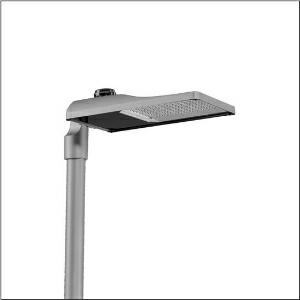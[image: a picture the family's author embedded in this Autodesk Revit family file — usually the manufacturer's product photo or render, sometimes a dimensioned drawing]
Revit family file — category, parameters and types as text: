
# Revit family: streetlight_sl_31_maxi___st1_5a_5xh8p7bn08sa_f059
name_source: partatom
category: Lighting Fixtures
units: mm (PartAtom-declared; Revit-internal decimal feet)

## family parameters
Cut with Voids When Loaded = No
Host = Face
Light Source = No
Part Type = Normal
Room Calculation Point = No
Round Connector Dimension = Use Diameter
Shared = No

## types (1)
- --- (1 x LED, 22010 lm, 208.6 W, 2200K)
    Apparent Load = 209 VA
    CIE Flux Codes = 22 53 95 100 100
    Color Rendering = 70
    Color Temperature = 2200K
    Default Elevation = 1800 mm
    Description = Streetlight SL 31 maxi NEMA (7pin) mast luminaire for post-top, side-entry; light control with lens of PMMA; light distribution: ST1.5a, direct asymmetric distribution, for standard-compliant lighting for roads and squares; LED: luminous flux: 22.010lm, light colour: 722, colour temperature: 2200K; luminous efficacy: 105,5lm/W; control: pre-setting: linear dimming characteristic, flexible luminous flux parameterisation, time-dependent luminous flux control, constant luminous flux control, intelligent temperature release in ECG and LED module, overheat protection; luminaire housing, of diecast aluminium, SITECO metallic grey (DB 702S), corrosivity category C5 high according to DIN EN ISO 12944; cover of toughened safety glass, transparent, opened without tools; mast flange of diecast aluminium, SITECO metallic grey (DB 702S), spigot size: 76/60mm, mast flange included unmounted; with cable H07RN-F 3x 1.5mm², cable length: 14,5m, connection cable pre-assembled; mains connection: 220..240V, AC, 50/60Hz; power consumption (at start of service life): 208,6W / (at end of service life): 233,1W / (with reduced operation 50%): 88W; protection rating (complete): IP66; insulation class (complete): insulation class I (protective earthing); impact resistance: IK10; certification: CE, ENEC, ENEC+, VDE, UKCA; permissible operating ambient temperature for outdoor applications: -40..+50°C; packaging unit: 1 piece

Light Distribution: ST1.5a
    Height = 79 mm
    Lamp = 1 x LED
    Lamp Light Flux = 22010 lm
    Lamp Power = 208.6 W
    Lamp count = 1
    Length = 657 mm
    Luminous efficacy = 106 lm/W
    Manufacturer = Siteco
    ModVariant = No
    Model = 5XH8P7BN08SA
    Number of Poles = 1
    OnlyDefault = Yes
    Power Factor = 1
    Product Name = Streetlight SL 31 maxi | ST1.5a
    Product group = mast luminaire | pylon top
    ProductGroupID = 6100
    Protection Class = Protection class I
    Protection Degree = IP 66
    RLX_Detail_Level = 1
    RLX_Emergency_Light_Flux = 0 lm
    RLX_Emergency_Type = 0
    RLX_Emergency_Type_DB = No
    RlxData = <blob elided: 30473 chars, md5=b055d9e3>
    Socket = socket
    Standby Power = 0 W
    System Light Flux = 22009 lm
    System Power = 209 W
    Type Comments = factory setting: luminous flux: 100 % | dim-lin: 254 | 718 mA
    Type Image = l_1300293.jpg
    URL = http://relux.com
    VarID = @adj_008907
    Voltage = 0 V
    Weight = 0.00 kg
    Width = 362 mm

## geometry (parser evidence)
native form markers: Blend x4, Sweep x10
no freeform markers — native parametric forms only
